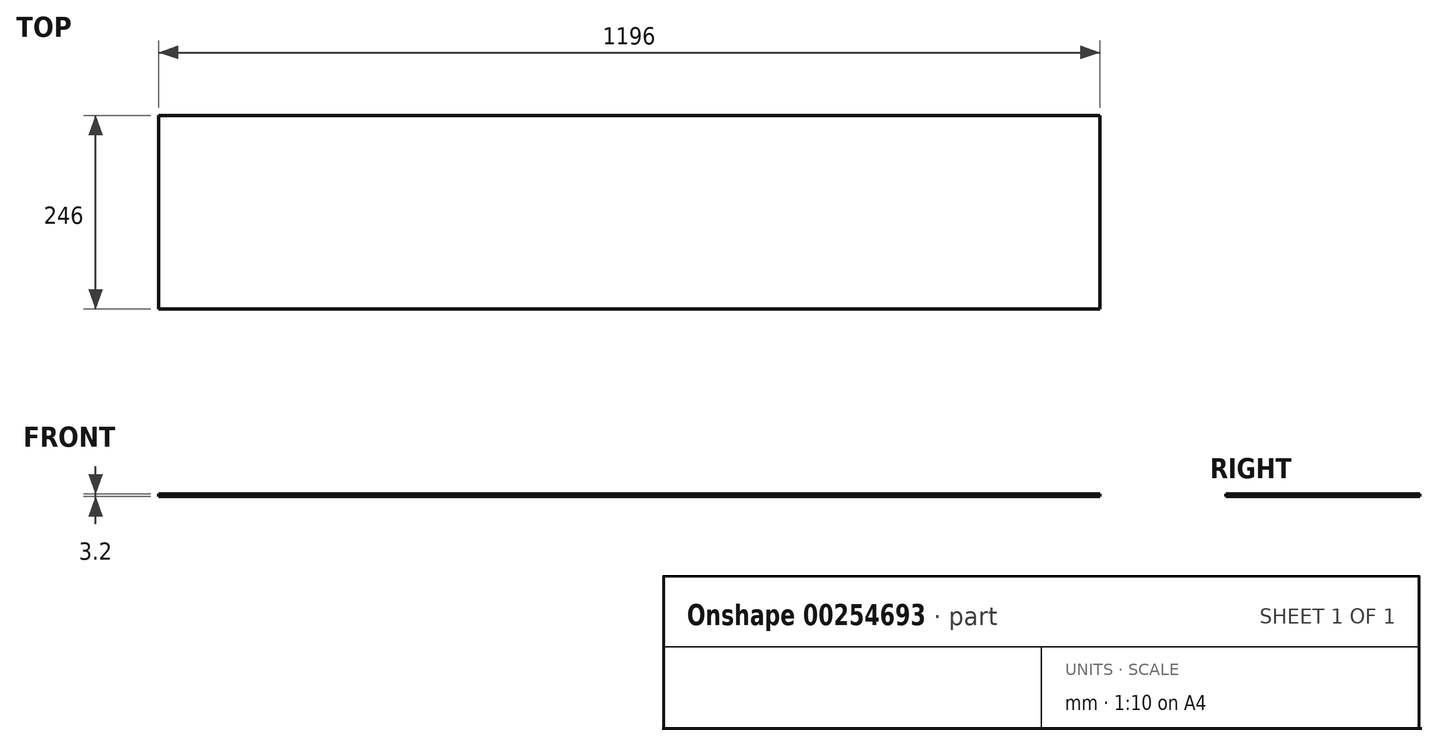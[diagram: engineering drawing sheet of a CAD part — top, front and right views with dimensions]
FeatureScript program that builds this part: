
annotation { "Feature Type Name" : "Feature", "Feature Type Description" : "" }
export const myFeature = defineFeature(function(context is Context, id is Id, definition is map)
    precondition{}
    {
        {
            var Q0;
            Q0=qCreatedBy(makeId("Top.planeOp"),FACE);
            var sketch = newSketch(context, id + "F0", { "sketchPlane" : qUnion([Q0])});
            skLineSegment(sketch, "E0.bottom", {"start": v(0, 0) * mm, "end": v(1196, 0) * mm});
            skLineSegment(sketch, "E0.top", {"start": v(0, 246) * mm, "end": v(1196, 246) * mm});
            skLineSegment(sketch, "E0.left", {"start": v(0, 0) * mm, "end": v(0, 246) * mm});
            skLineSegment(sketch, "E0.right", {"start": v(1196, 0) * mm, "end": v(1196, 246) * mm});
            skSolve(sketch);
        }
        {
            var Q0;
            Q0=qSketchRegion(id+"F0",true);
            extrude(context, id + "F1", {"entities" : qUnion([Q0]), "depth" : 3.2 * mm});
        }
    });
